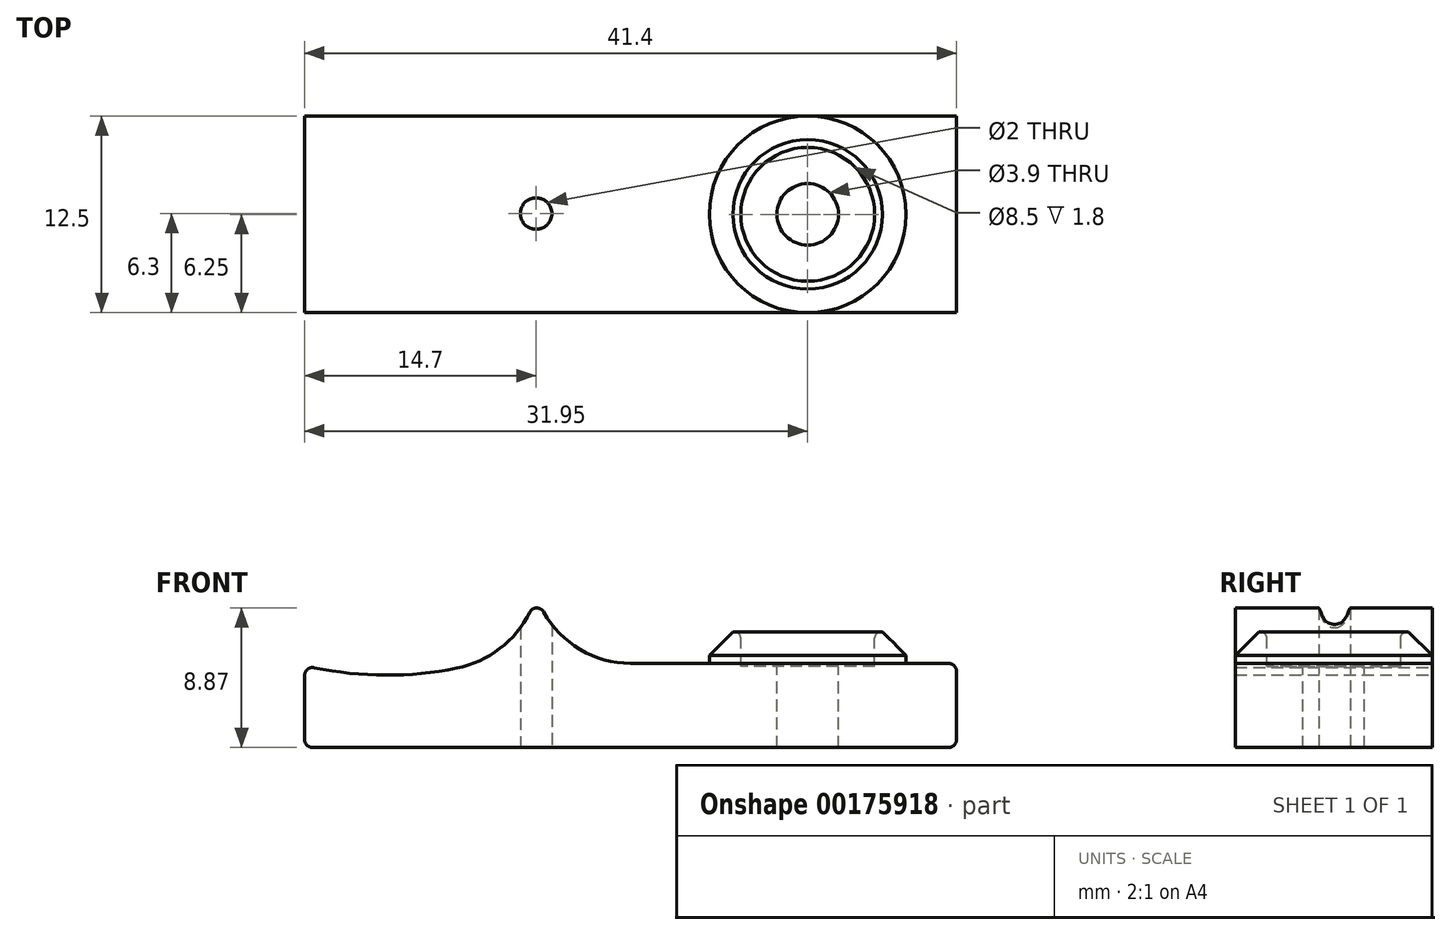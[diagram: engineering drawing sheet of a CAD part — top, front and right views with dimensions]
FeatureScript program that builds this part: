
annotation { "Feature Type Name" : "Feature", "Feature Type Description" : "" }
export const myFeature = defineFeature(function(context is Context, id is Id, definition is map)
    precondition{}
    {
        {
            var Q0;
            Q0=qCreatedBy(makeId("Front.planeOp"),FACE);
            var sketch = newSketch(context, id + "F0", { "sketchPlane" : qUnion([Q0])});
            skCircle(sketch, "E0", {"center": v(0, 0) * mm, "radius": 1.65 * mm});
            skCircle(sketch, "E1", {"center": v(2.25, -15.74) * mm, "radius": 1.65 * mm});
            skCircle(sketch, "E2", {"center": v(2.25, -15.74) * mm, "radius": 6.35 * mm});
            skLineSegment(sketch, "E3", {"start": v(-5.5, 5.15) * mm, "end": v(36.5, 5.15) * mm});
            skLineSegment(sketch, "E4", {"start": v(-5.5, 5.15) * mm, "end": v(-5.5, -21.85) * mm});
            skCircle(sketch, "E5", {"center": v(0, -31) * mm, "radius": 1.65 * mm});
            skLineSegment(sketch, "E6", {"start": v(-5.5, -27.15) * mm, "end": v(36.5, -27.15) * mm});
            skLineSegment(sketch, "E7", {"start": v(-5.5, -5.45) * mm, "end": v(36.5, -5.45) * mm});
            skPoint(sketch, "E8", {"position": v(15.5, -15.5) * mm});
            skCircle(sketch, "E9.1.0.0", {"center": v(31, 0) * mm, "radius": 1.65 * mm});
            skCircle(sketch, "E9.1.0.1", {"center": v(31, -31) * mm, "radius": 1.65 * mm});
            skLineSegment(sketch, "E9.direction1", {"start": v(0, -31) * mm, "end": v(31, -31) * mm, "construction": true});
            skLineSegment(sketch, "E10", {"start": v(9.5, 5.15) * mm, "end": v(9.5, -27.15) * mm, "construction": true});
            skLineSegment(sketch, "E11", {"start": v(26.75, 5.15) * mm, "end": v(26.75, -27.15) * mm, "construction": true});
            skLineSegment(sketch, "E12", {"start": v(-5.5, -27.15) * mm, "end": v(-5.5, -21.56) * mm});
            skLineSegment(sketch, "E13", {"start": v(15.5, -21.5) * mm, "end": v(36.5, -21.5) * mm});
            skLineSegment(sketch, "E14", {"start": v(36.5, -21.5) * mm, "end": v(36.5, -27.15) * mm});
            skArc(sketch, "E15", {"start": v(15.5, -21.5) * mm, "mid": v(19.73, -11.24) * mm, "end": v(9.5, -15.54) * mm});
            skArc(sketch, "E16", {"start": v(9.5, -15.54) * mm, "mid": v(9.5, -15.69) * mm, "end": v(9.5, -15.84) * mm});
            skArc(sketch, "E17", {"start": v(-5.5, -21.56) * mm, "mid": v(-1.63, -22.2) * mm, "end": v(2.3, -22.13) * mm});
            skArc(sketch, "E18", {"start": v(2.3, -22.13) * mm, "mid": v(3.35, -22) * mm, "end": v(4.4, -21.8) * mm});
            skArc(sketch, "E19", {"start": v(9.5, -15.84) * mm, "mid": v(11.38, -19.86) * mm, "end": v(15.5, -21.5) * mm});
            skArc(sketch, "E20", {"start": v(9.5, -15.54) * mm, "mid": v(-1.78, -11.58) * mm, "end": v(4.4, -21.8) * mm});
            skArc(sketch, "E21", {"start": v(4.4, -21.8) * mm, "mid": v(8.08, -19.59) * mm, "end": v(9.5, -15.54) * mm});
            skLineSegment(sketch, "E22.0", {"start": v(36.2, -21.8) * mm, "end": v(36.2, -27.15) * mm});
            skLineSegment(sketch, "E22.1", {"start": v(15.5, -21.8) * mm, "end": v(36.2, -21.8) * mm});
            skArc(sketch, "E22.2", {"start": v(9.52, -17.49) * mm, "mid": v(11.81, -20.6) * mm, "end": v(15.5, -21.8) * mm});
            skLineSegment(sketch, "E22.3", {"start": v(-5.2, -27.15) * mm, "end": v(-5.2, -21.94) * mm});
            skArc(sketch, "E22.4", {"start": v(-5.2, -21.94) * mm, "mid": v(-1.46, -22.5) * mm, "end": v(2.32, -22.43) * mm});
            skArc(sketch, "E22.5", {"start": v(2.32, -22.43) * mm, "mid": v(3.4, -22.3) * mm, "end": v(4.47, -22.1) * mm});
            skArc(sketch, "E22.6", {"start": v(4.47, -22.1) * mm, "mid": v(7.63, -20.5) * mm, "end": v(9.52, -17.49) * mm});
            skLineSegment(sketch, "E23", {"start": v(0, 0) * mm, "end": v(0, -15.9) * mm, "construction": true});
            skSolve(sketch);
        }
        {
            var Q0;
            {var subQ1=sQuery(id+"F0.wireOp",EDGE,"E22.0");Q0=makeQuery(id+"F0.imprint","IMPRINT",FACE,{"disambiguationData":[TD([[makeQuery(id+"F0.imprint","IMPRINT",EDGE,{"derivedFrom":subQ1}),-1.0]])]});}
            var Q1;
            {var subQ0=sQuery(id+"F0.wireOp",EDGE,"E22.6");var subQ1=sQuery(id+"F0.wireOp",EDGE,"418354bb-82ff-4c25-83f0-ff817fe12a48");var subQ2=makeQuery(id+"F0.imprint","INTERSECT",VERTEX,{"derivedFrom":[subQ1,subQ0]});Q1=makeQuery(id+"F0.imprint","IMPRINT",FACE,{"disambiguationData":[TD([[makeQuery(id+"F0.imprint","IMPRINT",EDGE,{"disambiguationData":[TD([[subQ2,-1.0]])],"derivedFrom":subQ1}),1.0]])]});}
            extrude(context, id + "F1", {"entities" : qUnion([Q0, Q1]), "depth" : 12.5 * mm});
        }
        {
            var Q0;
            Q0=makeQuery(id+"F1.opExtrude","SWEPT_EDGE",EDGE,{"disambiguationData":[OSD([sQuery(id+"F0.wireOp",EDGE,"E22.3"),sQuery(id+"F0.wireOp",EDGE,"E22.4")])]});
            var Q1;
            Q1=makeQuery(id+"F1.opExtrude","SWEPT_EDGE",EDGE,{"disambiguationData":[OSD([sQuery(id+"F0.wireOp",EDGE,"E6"),sQuery(id+"F0.wireOp",EDGE,"E22.3")])]});
            var Q2;
            Q2=makeQuery(id+"F1.opExtrude","SWEPT_EDGE",EDGE,{"disambiguationData":[OSD([sQuery(id+"F0.wireOp",EDGE,"E22.0"),sQuery(id+"F0.wireOp",EDGE,"E22.1")])]});
            var Q3;
            Q3=makeQuery(id+"F1.opExtrude","SWEPT_EDGE",EDGE,{"disambiguationData":[OSD([sQuery(id+"F0.wireOp",EDGE,"E6"),sQuery(id+"F0.wireOp",EDGE,"E22.0")])]});
            var Q4;
            Q4=makeQuery(id+"F1.opExtrude","SWEPT_EDGE",EDGE,{"disambiguationData":[OSD([sQuery(id+"F0.wireOp",EDGE,"E22.2"),sQuery(id+"F0.wireOp",EDGE,"E22.6")])]});
            fillet(context, id + "F2", {"entities" : qUnion([Q0, Q1, Q2, Q3, Q4]), "radius" : 0.5 * mm, "tangentPropagation" : true, "allowEdgeOverflow" : false});
        }
        {
            var Q0;
            Q0=makeQuery(id+"F1.opExtrude","SWEPT_FACE",FACE,{"disambiguationData":[OSD([sQuery(id+"F0.wireOp",EDGE,"E6")])]});
            cPlane(context, id + "F3", {"entities" : qUnion([Q0]), "cplaneType" : CPlaneType.OFFSET, "offset" : 0 * mm, "width" : 150 * mm, "height" : 150 * mm});
        }
        {
            var Q0;
            Q0=qCreatedBy(id+"F3.planeOp",FACE);
            var sketch = newSketch(context, id + "F4", { "sketchPlane" : qUnion([Q0])});
            skPoint(sketch, "E24", {"position": v(9.5, 6.2) * mm});
            skPoint(sketch, "E25", {"position": v(27, 6.2) * mm});
            skLineSegment(sketch, "E26", {"start": v(9.5, 6.2) * mm, "end": v(6.5, 6.2) * mm});
            skLineSegment(sketch, "E27", {"start": v(9.5, 6.2) * mm, "end": v(12.5, 6.2) * mm});
            skSolve(sketch);
        }
        {
            var Q0;
            Q0=sQuery(id+"F4.wireOp",VERTEX,"E24");
            var Q1;
            Q1=makeQuery(id+"F1.opExtrude","SWEPT_BODY",BODY,{"disambiguationData":[OSD([sQuery(id+"F0.wireOp",EDGE,"E6"),sQuery(id+"F0.wireOp",EDGE,"E22.0"),sQuery(id+"F0.wireOp",EDGE,"E22.1"),sQuery(id+"F0.wireOp",EDGE,"E22.2"),sQuery(id+"F0.wireOp",EDGE,"E22.3"),sQuery(id+"F0.wireOp",EDGE,"E22.4"),sQuery(id+"F0.wireOp",EDGE,"E22.5"),sQuery(id+"F0.wireOp",EDGE,"E22.6")])]});
            hole(context, id + "F5", {"style" : HoleStyle.SIMPLE, "endStyle" : HoleEndStyle.THROUGH, "holeDiameter" : 2 * mm, "locations" : qUnion([Q0]), "scope" : qUnion([Q1]), "isTappedThrough" : true});
        }
        {
            var Q0;
            Q0=makeQuery(id+"F1.opExtrude","SWEPT_FACE",FACE,{"disambiguationData":[OSD([sQuery(id+"F0.wireOp",EDGE,"E22.1")])]});
            cPlane(context, id + "F6", {"entities" : qUnion([Q0]), "cplaneType" : CPlaneType.OFFSET, "offset" : 0 * mm, "width" : 150 * mm, "height" : 150 * mm});
        }
        {
            var Q0;
            Q0=qCreatedBy(id+"F6.planeOp",FACE);
            var sketch = newSketch(context, id + "F7", { "sketchPlane" : qUnion([Q0])});
            skCircle(sketch, "E28", {"center": v(26.75, -6.25) * mm, "radius": 4.25 * mm});
            skCircle(sketch, "E29", {"center": v(26.75, -6.25) * mm, "radius": 6.25 * mm});
            skSolve(sketch);
        }
        {
            var Q0;
            Q0=sQuery(id+"F7.wireOp",VERTEX,"E28.center");
            var Q1;
            Q1=makeQuery(id+"F1.opExtrude","SWEPT_BODY",BODY,{"disambiguationData":[OSD([sQuery(id+"F0.wireOp",EDGE,"E6"),sQuery(id+"F0.wireOp",EDGE,"E22.0"),sQuery(id+"F0.wireOp",EDGE,"E22.1"),sQuery(id+"F0.wireOp",EDGE,"E22.2"),sQuery(id+"F0.wireOp",EDGE,"E22.3"),sQuery(id+"F0.wireOp",EDGE,"E22.4"),sQuery(id+"F0.wireOp",EDGE,"E22.5"),sQuery(id+"F0.wireOp",EDGE,"E22.6")])]});
            hole(context, id + "F8", {"style" : HoleStyle.C_BORE, "endStyle" : HoleEndStyle.THROUGH, "holeDiameter" : 3.9 * mm, "cBoreDiameter" : 8.5 * mm, "cBoreDepth" : 0.2 * mm, "locations" : qUnion([Q0]), "scope" : qUnion([Q1]), "isTappedThrough" : true});
        }
        {
            var Q0;
            Q0=makeQuery(id+"F7.imprint","IMPRINT",FACE,{"disambiguationData":[TD([[makeQuery(id+"F7.imprint","IMPRINT",EDGE,{"derivedFrom":sQuery(id+"F7.wireOp",EDGE,"E28")}),-1.0]])]});
            extrude(context, id + "F9", {"entities" : qUnion([Q0]), "operationType" : NewBodyOperationType.ADD, "depth" : 2 * mm});
        }
        {
            var Q0;
            Q0=makeQuery(id+"F5.hole-0.boolean.opBoolean","INTERSECT",EDGE,{"disambiguationData":[OD(0.0)],"derivedFrom":[makeQuery(id+"F2.opFillet","BLEND_FACE",FACE,{"disambiguationData":[OSD([sQuery(id+"F0.wireOp",EDGE,"E22.2"),sQuery(id+"F0.wireOp",EDGE,"E22.6")])]}),makeQuery(id+"F5.hole-0.opRevolve","SWEPT_FACE",FACE,{"disambiguationData":[OSD([sQuery(id+"F5.hole-0.sketch.wireOp",EDGE,"core_line_2")])]})]});
            var Q1;
            Q1=makeQuery(id+"F5.hole-0.boolean.opBoolean","INTERSECT",EDGE,{"disambiguationData":[OD(1.0)],"derivedFrom":[makeQuery(id+"F2.opFillet","BLEND_FACE",FACE,{"disambiguationData":[OSD([sQuery(id+"F0.wireOp",EDGE,"E22.2"),sQuery(id+"F0.wireOp",EDGE,"E22.6")])]}),makeQuery(id+"F5.hole-0.opRevolve","SWEPT_FACE",FACE,{"disambiguationData":[OSD([sQuery(id+"F5.hole-0.sketch.wireOp",EDGE,"core_line_2")])]})]});
            var Q2;
            Q2=makeQuery(id+"F8.hole-0.boolean.opBoolean","COPY",EDGE,{"derivedFrom":makeQuery(id+"F8.hole-0.opRevolve","SWEPT_EDGE",EDGE,{"disambiguationData":[OSD([sQuery(id+"F8.hole-0.sketch.wireOp",EDGE,"cbore_start_line_1"),sQuery(id+"F8.hole-0.sketch.wireOp",EDGE,"core_line_2")])]})});
            var Q3;
            Q3=makeQuery(id+"F9.opExtrude","CAP_EDGE",EDGE,{"disambiguationData":[OSD([sQuery(id+"F7.wireOp",EDGE,"E28")])],"isStart":false});
            fillet(context, id + "F10", {"entities" : qUnion([Q0, Q1, Q2, Q3]), "radius" : 0.4 * mm, "tangentPropagation" : true, "allowEdgeOverflow" : false});
        }
        {
            var Q0;
            Q0=makeQuery(id+"F9.opExtrude","CAP_EDGE",EDGE,{"disambiguationData":[OSD([sQuery(id+"F7.wireOp",EDGE,"E29")])],"isStart":false});
            chamfer(context, id + "F11", {"entities" : qUnion([Q0]), "width" : 1.5 * mm, "tangentPropagation" : true});
        }
    });
